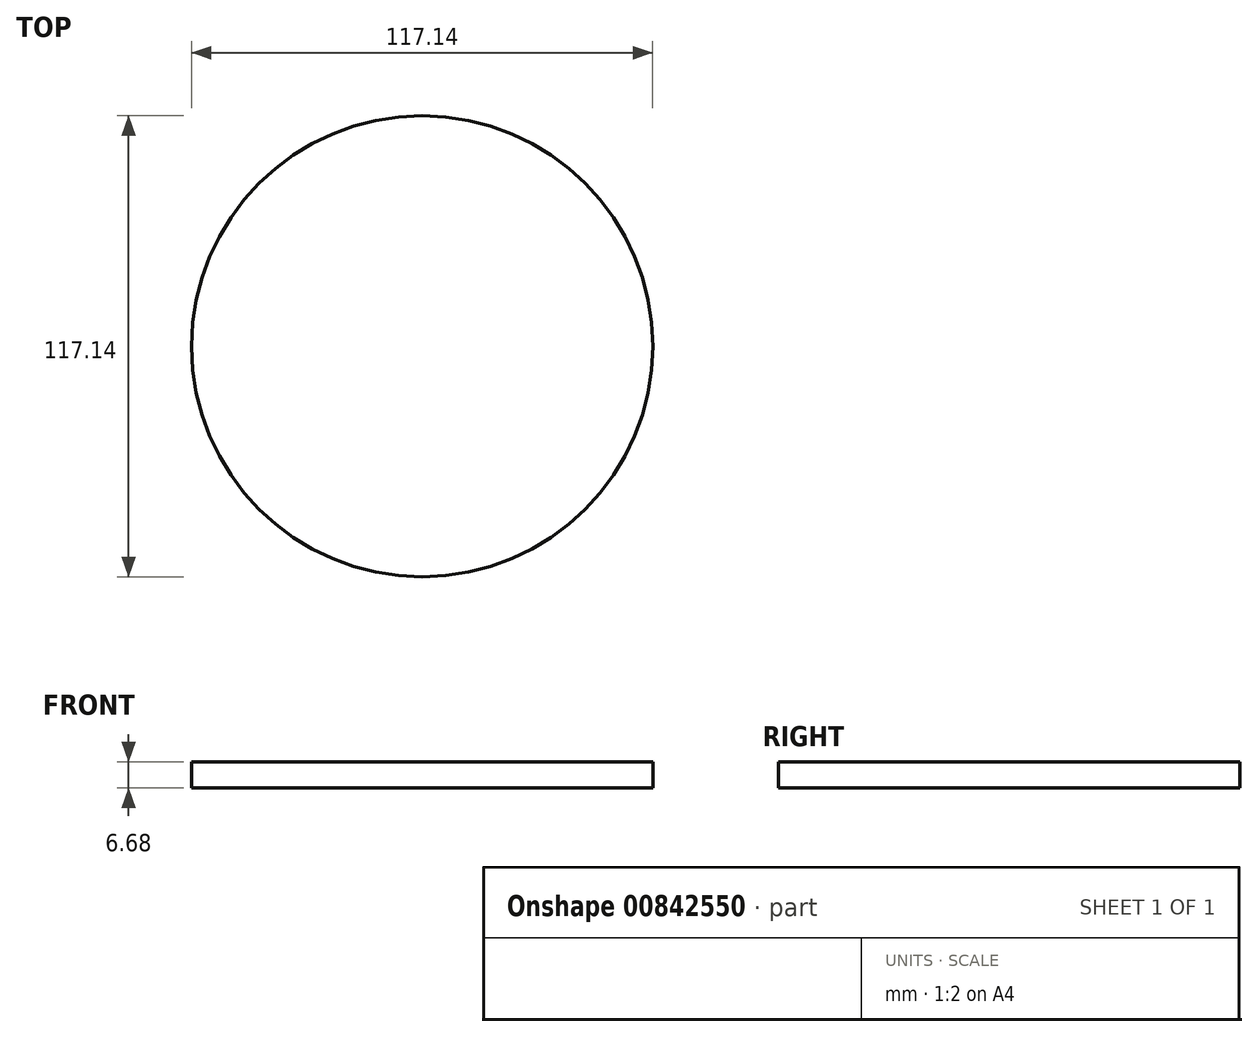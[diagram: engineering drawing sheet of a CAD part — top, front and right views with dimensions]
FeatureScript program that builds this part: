
annotation { "Feature Type Name" : "Feature", "Feature Type Description" : "" }
export const myFeature = defineFeature(function(context is Context, id is Id, definition is map)
    precondition{}
    {
        {
            var Q0;
            Q0=qCreatedBy(makeId("Top.planeOp"),FACE);
            var sketch = newSketch(context, id + "F0", { "sketchPlane" : qUnion([Q0])});
            skCircle(sketch, "E0", {"center": v(0, 0) * mm, "radius": 58.57 * mm});
            skSolve(sketch);
        }
        {
            var Q0;
            Q0 = qSketchRegion(id + "F0", true);
            extrude(context, id + "F1", {"entities" : qUnion([Q0]), "depth" : 6.68 * mm, "offsetDistance" : 25.4 * mm});
        }
    });
